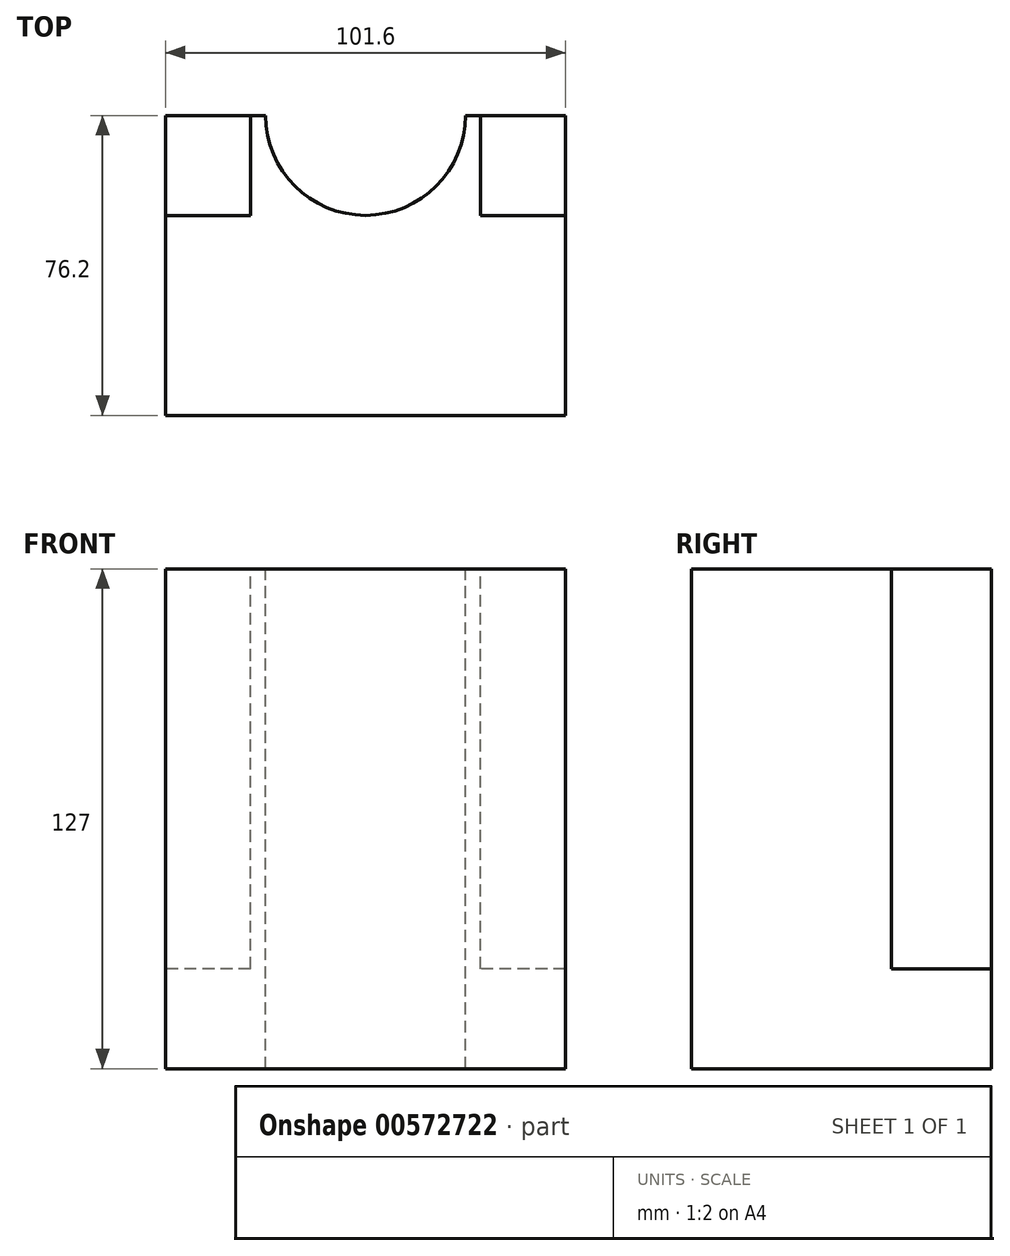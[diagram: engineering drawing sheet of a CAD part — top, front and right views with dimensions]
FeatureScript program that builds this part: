
annotation { "Feature Type Name" : "Feature", "Feature Type Description" : "" }
export const myFeature = defineFeature(function(context is Context, id is Id, definition is map)
    precondition{}
    {
        {
            var Q0;
            Q0=qCreatedBy(makeId("Top.planeOp"),FACE);
            var sketch = newSketch(context, id + "F0", { "sketchPlane" : qUnion([Q0])});
            skLineSegment(sketch, "E0.bottom", {"start": v(50.8, 38.1) * mm, "end": v(-50.8, 38.1) * mm});
            skLineSegment(sketch, "E0.top", {"start": v(50.8, -38.1) * mm, "end": v(-50.8, -38.1) * mm});
            skLineSegment(sketch, "E0.left", {"start": v(50.8, 38.1) * mm, "end": v(50.8, -38.1) * mm});
            skLineSegment(sketch, "E0.right", {"start": v(-50.8, 38.1) * mm, "end": v(-50.8, -38.1) * mm});
            skPoint(sketch, "E0.middle", {"position": v(0, 0) * mm});
            skSolve(sketch);
        }
        {
            var Q0;
            Q0=makeQuery(id+"F0.imprint","IMPRINT",FACE,{"disambiguationData":[TD([[makeQuery(id+"F0.imprint","IMPRINT",EDGE,{"derivedFrom":sQuery(id+"F0.wireOp",EDGE,"E0.bottom")}),1.0]])]});
            extrude(context, id + "F1", {"entities" : qUnion([Q0]), "depth" : 127 * mm, "offsetDistance" : 25.4 * mm});
        }
        {
            var Q0;
            Q0=makeQuery(id+"F1.opExtrude","CAP_FACE",FACE,{"disambiguationData":[OSD([sQuery(id+"F0.wireOp",EDGE,"E0.bottom"),sQuery(id+"F0.wireOp",EDGE,"E0.top"),sQuery(id+"F0.wireOp",EDGE,"E0.left"),sQuery(id+"F0.wireOp",EDGE,"E0.right")])],"isStart":false});
            var sketch = newSketch(context, id + "F2", { "sketchPlane" : qUnion([Q0])});
            skCircle(sketch, "E1", {"center": v(0, 38.1) * mm, "radius": 25.4 * mm});
            skSolve(sketch);
        }
        {
            var Q0;
            {var subQ0=sQuery(id+"F2.wireOp",EDGE,"E1");var subQ1=makeQuery(id+"F1.opExtrude","CAP_EDGE",EDGE,{"disambiguationData":[OSD([sQuery(id+"F0.wireOp",EDGE,"E0.bottom")])],"isStart":false});var subQ2=makeQuery(id+"F2.imprint","INTERSECT",VERTEX,{"disambiguationData":[OD(0.0)],"derivedFrom":[subQ1,subQ0]});Q0=makeQuery(id+"F2.imprint","IMPRINT",FACE,{"disambiguationData":[TD([[makeQuery(id+"F2.imprint","IMPRINT",EDGE,{"disambiguationData":[TD([[subQ2,1.0]])],"derivedFrom":subQ0}),1.0]])]});}
            extrude(context, id + "F3", {"entities" : qUnion([Q0]), "operationType" : NewBodyOperationType.REMOVE, "endBound" : BoundingType.THROUGH_ALL, "oppositeDirection" : true, "depth" : 25.4 * mm, "offsetDistance" : 25.4 * mm});
        }
        {
            var Q0;
            Q0=makeQuery(id+"F1.opExtrude","CAP_FACE",FACE,{"disambiguationData":[OSD([sQuery(id+"F0.wireOp",EDGE,"E0.bottom"),sQuery(id+"F0.wireOp",EDGE,"E0.top"),sQuery(id+"F0.wireOp",EDGE,"E0.left"),sQuery(id+"F0.wireOp",EDGE,"E0.right")])],"isStart":false});
            var sketch = newSketch(context, id + "F4", { "sketchPlane" : qUnion([Q0])});
            skLineSegment(sketch, "E2.bottom", {"start": v(-50.8, 38.1) * mm, "end": v(-29.21, 38.1) * mm});
            skLineSegment(sketch, "E2.top", {"start": v(-50.8, 12.7) * mm, "end": v(-29.21, 12.7) * mm});
            skLineSegment(sketch, "E2.left", {"start": v(-50.8, 38.1) * mm, "end": v(-50.8, 12.7) * mm});
            skLineSegment(sketch, "E2.right", {"start": v(-29.21, 38.1) * mm, "end": v(-29.21, 12.7) * mm});
            skLineSegment(sketch, "E3.MirrorCS", {"start": v(50.8, 38.1) * mm, "end": v(50.8, 12.7) * mm});
            skLineSegment(sketch, "E4.MirrorCS", {"start": v(50.8, 12.7) * mm, "end": v(29.21, 12.7) * mm});
            skLineSegment(sketch, "E5.MirrorCS", {"start": v(50.8, 38.1) * mm, "end": v(29.21, 38.1) * mm});
            skLineSegment(sketch, "E6.MirrorCS", {"start": v(29.21, 38.1) * mm, "end": v(29.21, 12.7) * mm});
            skSolve(sketch);
        }
        {
            var Q0;
            Q0=makeQuery(id+"F4.imprint","IMPRINT",FACE,{"disambiguationData":[TD([[makeQuery(id+"F4.imprint","IMPRINT",EDGE,{"derivedFrom":sQuery(id+"F4.wireOp",EDGE,"E2.bottom")}),1.0]])]});
            var Q1;
            Q1=makeQuery(id+"F4.imprint","IMPRINT",FACE,{"disambiguationData":[TD([[makeQuery(id+"F4.imprint","IMPRINT",EDGE,{"derivedFrom":sQuery(id+"F4.wireOp",EDGE,"E3.MirrorCS")}),-1.0]])]});
            extrude(context, id + "F5", {"entities" : qUnion([Q0, Q1]), "operationType" : NewBodyOperationType.REMOVE, "oppositeDirection" : true, "depth" : 101.6 * mm, "offsetDistance" : 25.4 * mm});
        }
    });
